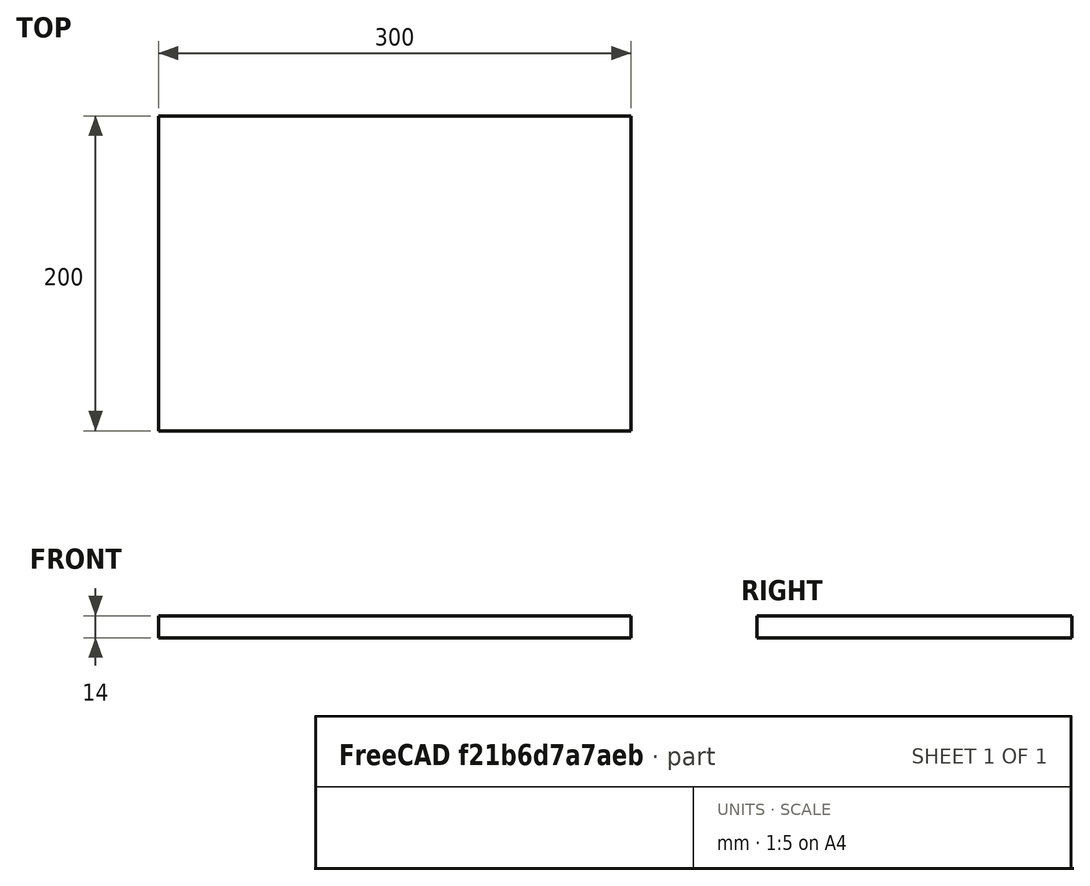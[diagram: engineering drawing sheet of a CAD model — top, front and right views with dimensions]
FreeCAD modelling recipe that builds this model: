
FCSTD DOCUMENT  (FreeCAD 0.19R24276 (Git))
Label: Plate_300x200
License: All rights reserved
LicenseURL: http://en.wikipedia.org/wiki/All_rights_reserved
objects: Sketcher::SketchObject×1, PartDesign::Pad×1, PartDesign::Body×1
note: 4 computed .brp shape members not serialized (recipe doc carries the construction recipe); baked Part::Feature solids carry a one-line shape summary decoded from their .brp

FEATURE [Sketcher::SketchObject] Sketch
  FullyConstrained = true
  MapMode = 5
  Support = -> [XY_Plane]
  sketch-geometry (4):
    g0: LineSegment StartX=0 StartY=0 StartZ=0 EndX=300 EndY=0 EndZ=0
    g1: LineSegment StartX=300 StartY=0 StartZ=0 EndX=300 EndY=200 EndZ=0
    g2: LineSegment StartX=300 StartY=200 StartZ=0 EndX=0 EndY=200 EndZ=0
    g3: LineSegment StartX=0 StartY=200 StartZ=0 EndX=0 EndY=0 EndZ=0
  constraints (11):
    c: Coincident(g0,g1)
    c: Coincident(g1,g2)
    c: Coincident(g2,g3)
    c: Coincident(g3,g0)
    c: Horizontal(g0)
    c: Horizontal(g2)
    c: Vertical(g1)
    c: Vertical(g3)
    c: Coincident(g0,g-1)
    c: DistanceX(g0,g0) = 300
    c: DistanceY(g3,g3) = 200
FEATURE [PartDesign::Pad] Pad
  Direction = (1,1,1)
  Length = 14
  Length2 = 100
  Profile = -> Sketch
  Type = 0
FEATURE [PartDesign::Body] Body
  Group = -> [Sketch,Pad]
  Origin = -> Origin
  Tip = -> Pad
